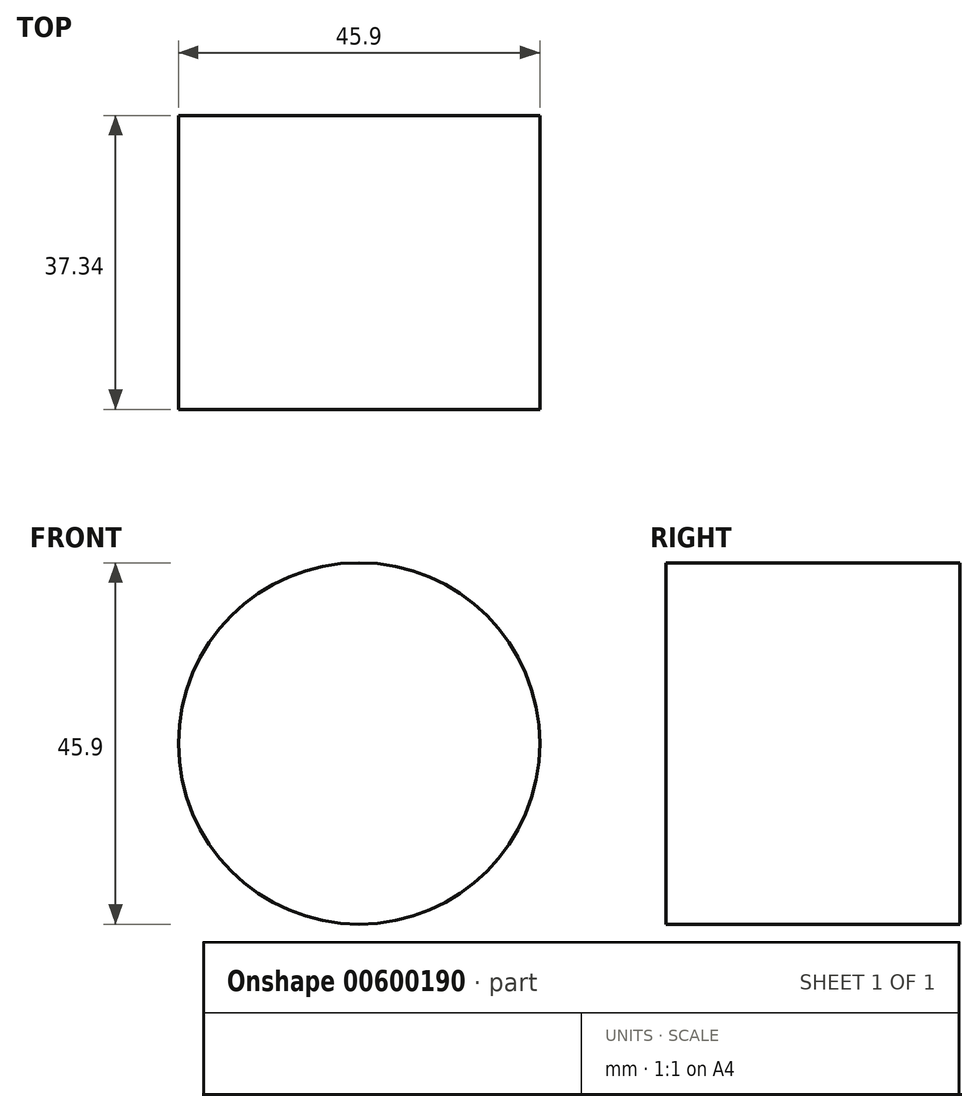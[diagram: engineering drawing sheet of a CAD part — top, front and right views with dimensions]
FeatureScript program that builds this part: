
annotation { "Feature Type Name" : "Feature", "Feature Type Description" : "" }
export const myFeature = defineFeature(function(context is Context, id is Id, definition is map)
    precondition{}
    {
        {
            var Q0;
            Q0=qCreatedBy(makeId("Front.planeOp"),FACE);
            var sketch = newSketch(context, id + "F0", { "sketchPlane" : qUnion([Q0])});
            skCircle(sketch, "E0", {"center": v(0, 0) * mm, "radius": 22.95 * mm});
            skSolve(sketch);
        }
        {
            var Q0;
            Q0=makeQuery(id+"F0.imprint","IMPRINT",FACE,{"disambiguationData":[TD([[makeQuery(id+"F0.imprint","IMPRINT",EDGE,{"derivedFrom":sQuery(id+"F0.wireOp",EDGE,"E0")}),1.0]])]});
            extrude(context, id + "F1", {"entities" : qUnion([Q0]), "depth" : 37.34 * mm, "offsetDistance" : 25.4 * mm});
        }
    });
